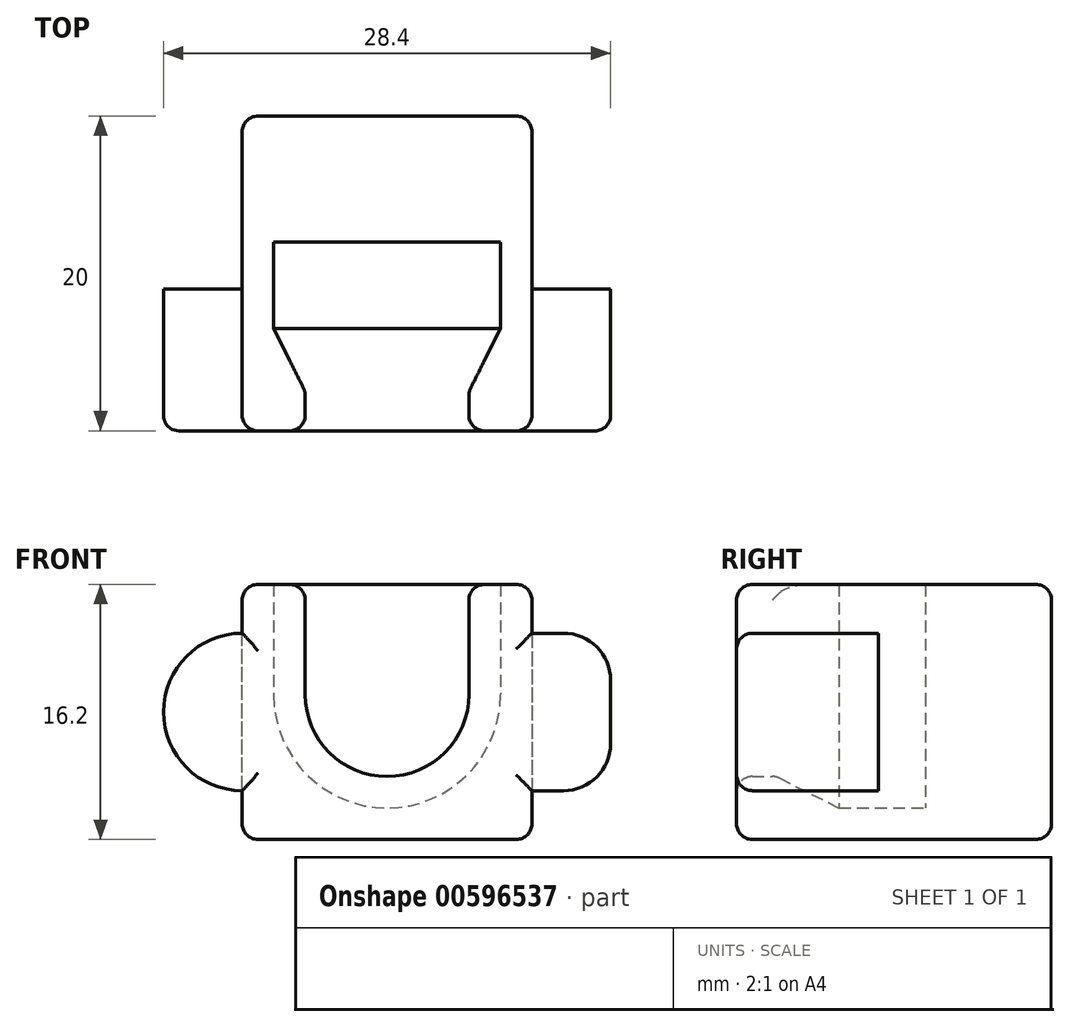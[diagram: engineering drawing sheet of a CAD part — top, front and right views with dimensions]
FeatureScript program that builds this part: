
annotation { "Feature Type Name" : "Feature", "Feature Type Description" : "" }
export const myFeature = defineFeature(function(context is Context, id is Id, definition is map)
    precondition{}
    {
        {
            var Q0;
            Q0=qCreatedBy(makeId("Top.planeOp"),FACE);
            var sketch = newSketch(context, id + "F0", { "sketchPlane" : qUnion([Q0])});
            skLineSegment(sketch, "E0", {"start": v(-9.2, 0) * mm, "end": v(-5.2, 0) * mm});
            skLineSegment(sketch, "E1", {"start": v(-5.2, 0) * mm, "end": v(-5.2, 2.5) * mm});
            skLineSegment(sketch, "E2", {"start": v(-5.2, 2.5) * mm, "end": v(-7.2, 6.5) * mm});
            skLineSegment(sketch, "E3", {"start": v(-7.2, 6.5) * mm, "end": v(-7.2, 12) * mm});
            skLineSegment(sketch, "E4", {"start": v(-7.2, 12) * mm, "end": v(0, 12) * mm});
            skLineSegment(sketch, "E5", {"start": v(0, 12) * mm, "end": v(0, 14) * mm});
            skLineSegment(sketch, "E6", {"start": v(0, 14) * mm, "end": v(-9.2, 14) * mm});
            skLineSegment(sketch, "E7", {"start": v(-9.2, 14) * mm, "end": v(-9.2, 0) * mm});
            skLineSegment(sketch, "E8", {"start": v(0, 44.18) * mm, "end": v(0, -54.71) * mm, "construction": true});
            skSolve(sketch);
        }
        {
            var Q0;
            Q0=makeQuery(id+"F0.imprint","IMPRINT",FACE,{"disambiguationData":[TD([[makeQuery(id+"F0.imprint","IMPRINT",EDGE,{"derivedFrom":sQuery(id+"F0.wireOp",EDGE,"E0")}),1.0]])]});
            var Q1;
            Q1=sQuery(id+"F0.wireOp",EDGE,"E8");
            revolve(context, id + "F1", {"entities" : qUnion([Q0]), "axis" : qUnion([Q1]), "revolveType" : RevolveType.ONE_DIRECTION, "angle" : 180 * degree});
        }
        {
            var Q0;
            Q0=makeQuery(id+"F1.opRevolve","SWEPT_FACE",FACE,{"disambiguationData":[OSD([sQuery(id+"F0.wireOp",EDGE,"E6")])]});
            var sketch = newSketch(context, id + "F2", { "sketchPlane" : qUnion([Q0])});
            skLineSegment(sketch, "E9", {"start": v(-9.2, 0) * mm, "end": v(-9.2, -9.2) * mm});
            skPoint(sketch, "E9.endSnap0", {"position": v(0, -9.2) * mm});
            skLineSegment(sketch, "E10", {"start": v(-9.2, -9.2) * mm, "end": v(9.2, -9.2) * mm});
            skLineSegment(sketch, "E11", {"start": v(9.2, -9.2) * mm, "end": v(9.2, 0) * mm});
            skSolve(sketch);
        }
        {
            var Q0;
            {var subQ0=sQuery(id+"F2.wireOp",EDGE,"E9");Q0=makeQuery(id+"F2.imprint","IMPRINT",FACE,{"disambiguationData":[TD([[makeQuery(id+"F2.imprint","IMPRINT",EDGE,{"derivedFrom":subQ0}),1.0]])]});}
            var Q1;
            {var subQ0=sQuery(id+"F2.wireOp",EDGE,"E11");Q1=makeQuery(id+"F2.imprint","IMPRINT",FACE,{"disambiguationData":[TD([[makeQuery(id+"F2.imprint","IMPRINT",EDGE,{"derivedFrom":subQ0}),1.0]])]});}
            var Q2;
            Q2=makeQuery(id+"F1.opRevolve","SWEPT_FACE",FACE,{"disambiguationData":[OSD([sQuery(id+"F0.wireOp",EDGE,"E0")])]});
            extrude(context, id + "F3", {"entities" : qUnion([Q0, Q1]), "operationType" : NewBodyOperationType.ADD, "endBound" : BoundingType.UP_TO_SURFACE, "oppositeDirection" : true, "depth" : 17 * mm, "endBoundEntityFace" : qUnion([Q2]), "offsetDistance" : 25 * mm});
        }
        {
            var Q0;
            Q0=makeQuery(id+"F1.opRevolve","CAP_FACE",FACE,{"disambiguationData":[OSD([sQuery(id+"F0.wireOp",EDGE,"E0"),sQuery(id+"F0.wireOp",EDGE,"E1"),sQuery(id+"F0.wireOp",EDGE,"E2"),sQuery(id+"F0.wireOp",EDGE,"E3"),sQuery(id+"F0.wireOp",EDGE,"E4"),sQuery(id+"F0.wireOp",EDGE,"E5"),sQuery(id+"F0.wireOp",EDGE,"E6"),sQuery(id+"F0.wireOp",EDGE,"E7")])],"isStart":false});
            extrude(context, id + "F4", {"entities" : qUnion([Q0]), "operationType" : NewBodyOperationType.ADD, "depth" : 7 * mm, "offsetDistance" : 25 * mm});
        }
        {
            var Q0;
            {var subQ0=sQuery(id+"F0.wireOp",EDGE,"E6");var subQ1=sQuery(id+"F2.wireOp",EDGE,"E10");var subQ2=sQuery(id+"F0.wireOp",EDGE,"E7");Q0=makeQuery(id+"F4.boolean.opBoolean","MERGE",FACE,{"derivedFrom":[makeQuery(id+"F3.boolean.opBoolean","MERGE",FACE,{"derivedFrom":[makeQuery(id+"F1.opRevolve","SWEPT_FACE",FACE,{"disambiguationData":[OSD([subQ0])]}),makeQuery(id+"F3.opExtrude","CAP_FACE",FACE,{"disambiguationData":[OSD([subQ0,subQ2,sQuery(id+"F2.wireOp",EDGE,"E9"),subQ1])],"isStart":true}),makeQuery(id+"F3.opExtrude","CAP_FACE",FACE,{"disambiguationData":[OSD([subQ0,subQ2,subQ1,sQuery(id+"F2.wireOp",EDGE,"E11")])],"isStart":true})]}),makeQuery(id+"F4.opExtrude","SWEPT_FACE",FACE,{"disambiguationData":[OSD([subQ0])]})]});}
            var sketch = newSketch(context, id + "F5", { "sketchPlane" : qUnion([Q0])});
            skCircle(sketch, "E12", {"center": v(9.2, -1.1) * mm, "radius": 5 * mm});
            skLineSegment(sketch, "E13.bottom", {"start": v(-11.2, 3.9) * mm, "end": v(-4.2, 3.9) * mm});
            skLineSegment(sketch, "E13.top", {"start": v(-11.2, -6.1) * mm, "end": v(-4.2, -6.1) * mm});
            skLineSegment(sketch, "E13.left", {"start": v(-14.2, 0.9) * mm, "end": v(-14.2, -3.1) * mm});
            skLineSegment(sketch, "E13.right", {"start": v(-4.2, 3.9) * mm, "end": v(-4.2, -6.1) * mm});
            skPoint(sketch, "E13.middle", {"position": v(-9.2, -1.1) * mm});
            skPoint(sketch, "E14.visualSharp", {"position": v(-14.2, -6.1) * mm});
            skArc(sketch, "E14.filletArc", {"start": v(-14.2, -3.1) * mm, "mid": v(-13.32, -5.22) * mm, "end": v(-11.2, -6.1) * mm});
            skPoint(sketch, "E15.visualSharp", {"position": v(-14.2, 3.9) * mm});
            skArc(sketch, "E15.filletArc", {"start": v(-11.2, 3.9) * mm, "mid": v(-13.32, 3.02) * mm, "end": v(-14.2, 0.9) * mm});
            skSolve(sketch);
        }
        {
            var Q0;
            {var subQ0=sQuery(id+"F5.wireOp",EDGE,"E12");var subQ1=sQuery(id+"F2.wireOp",EDGE,"E11");var subQ2=makeQuery(id+"F4.boolean.opBoolean","MERGE",EDGE,{"derivedFrom":[makeQuery(id+"F3.opExtrude","CAP_EDGE",EDGE,{"disambiguationData":[OSD([subQ1])],"isStart":true}),makeQuery(id+"F4.opExtrude","SWEPT_EDGE",EDGE,{"disambiguationData":[OSD([sQuery(id+"F0.wireOp",EDGE,"E6"),sQuery(id+"F0.wireOp",EDGE,"E7"),subQ1])]})]});var subQ3=makeQuery(id+"F5.imprint","INTERSECT",VERTEX,{"disambiguationData":[OD(0.0)],"derivedFrom":[subQ2,subQ0]});Q0=makeQuery(id+"F5.imprint","IMPRINT",FACE,{"disambiguationData":[TD([[makeQuery(id+"F5.imprint","IMPRINT",EDGE,{"disambiguationData":[TD([[subQ3,-1.0]])],"derivedFrom":subQ0}),1.0]])]});}
            var Q1;
            Q1=makeQuery(id+"F5.imprint","IMPRINT",FACE,{"disambiguationData":[TD([[makeQuery(id+"F5.imprint","IMPRINT",EDGE,{"derivedFrom":sQuery(id+"F5.wireOp",EDGE,"E13.left")}),1.0]])]});
            var Q2;
            {var subQ0=sQuery(id+"F0.wireOp",EDGE,"E0");Q2=makeQuery(id+"F4.boolean.opBoolean","MERGE",FACE,{"derivedFrom":[makeQuery(id+"F3.boolean.opBoolean","MERGE",FACE,{"derivedFrom":[makeQuery(id+"F1.opRevolve","SWEPT_FACE",FACE,{"disambiguationData":[OSD([subQ0])]}),makeQuery(id+"F3.opExtrude","CAP_FACE",FACE,{"disambiguationData":[OSD([subQ0]),OD(0.0)],"isStart":false}),makeQuery(id+"F3.opExtrude","CAP_FACE",FACE,{"disambiguationData":[OSD([subQ0]),OD(1.0)],"isStart":false})]}),makeQuery(id+"F4.opExtrude","SWEPT_FACE",FACE,{"disambiguationData":[OSD([subQ0]),TDD([makeQuery(id+"F1.opRevolve","CAP_EDGE",EDGE,{"disambiguationData":[OSD([subQ0])],"isStart":true})])]}),makeQuery(id+"F4.opExtrude","SWEPT_FACE",FACE,{"disambiguationData":[OSD([subQ0]),TDD([makeQuery(id+"F1.opRevolve","CAP_EDGE",EDGE,{"disambiguationData":[OSD([subQ0])],"isStart":false})])]})]});}
            extrude(context, id + "F6", {"entities" : qUnion([Q0, Q1]), "operationType" : NewBodyOperationType.ADD, "endBound" : BoundingType.UP_TO_SURFACE, "oppositeDirection" : true, "depth" : 25 * mm, "endBoundEntityFace" : qUnion([Q2]), "offsetDistance" : 25 * mm});
        }
        {
            var Q0;
            {var subQ0=sQuery(id+"F5.wireOp",EDGE,"E12");var subQ1=sQuery(id+"F2.wireOp",EDGE,"E11");var subQ2=makeQuery(id+"F4.boolean.opBoolean","MERGE",EDGE,{"derivedFrom":[makeQuery(id+"F3.opExtrude","CAP_EDGE",EDGE,{"disambiguationData":[OSD([subQ1])],"isStart":true}),makeQuery(id+"F4.opExtrude","SWEPT_EDGE",EDGE,{"disambiguationData":[OSD([sQuery(id+"F0.wireOp",EDGE,"E6"),sQuery(id+"F0.wireOp",EDGE,"E7"),subQ1])]})]});var subQ3=makeQuery(id+"F5.imprint","INTERSECT",VERTEX,{"disambiguationData":[OD(0.0)],"derivedFrom":[subQ2,subQ0]});Q0=makeQuery(id+"F5.imprint","IMPRINT",FACE,{"disambiguationData":[TD([[makeQuery(id+"F5.imprint","IMPRINT",EDGE,{"disambiguationData":[TD([[subQ3,-1.0]])],"derivedFrom":subQ0}),1.0]])]});}
            var Q1;
            Q1=makeQuery(id+"F5.imprint","IMPRINT",FACE,{"disambiguationData":[TD([[makeQuery(id+"F5.imprint","IMPRINT",EDGE,{"derivedFrom":sQuery(id+"F5.wireOp",EDGE,"E13.left")}),1.0]])]});
            extrude(context, id + "F7", {"entities" : qUnion([Q0, Q1]), "operationType" : NewBodyOperationType.REMOVE, "oppositeDirection" : true, "depth" : 5 * mm, "offsetDistance" : 25 * mm});
        }
        {
            var Q0;
            {var subQ0=sQuery(id+"F5.wireOp",EDGE,"E12");var subQ1=sQuery(id+"F2.wireOp",EDGE,"E11");var subQ2=makeQuery(id+"F4.boolean.opBoolean","MERGE",EDGE,{"derivedFrom":[makeQuery(id+"F3.opExtrude","CAP_EDGE",EDGE,{"disambiguationData":[OSD([subQ1])],"isStart":true}),makeQuery(id+"F4.opExtrude","SWEPT_EDGE",EDGE,{"disambiguationData":[OSD([sQuery(id+"F0.wireOp",EDGE,"E6"),sQuery(id+"F0.wireOp",EDGE,"E7"),subQ1])]})]});var subQ3=makeQuery(id+"F5.imprint","INTERSECT",VERTEX,{"disambiguationData":[OD(0.0)],"derivedFrom":[subQ2,subQ0]});Q0=makeQuery(id+"F5.imprint","IMPRINT",FACE,{"disambiguationData":[TD([[makeQuery(id+"F5.imprint","IMPRINT",EDGE,{"disambiguationData":[TD([[subQ3,1.0]])],"derivedFrom":subQ0}),1.0]])]});}
            var Q1;
            {var subQ0=sQuery(id+"F5.wireOp",EDGE,"E13.right");Q1=makeQuery(id+"F5.imprint","IMPRINT",FACE,{"disambiguationData":[TD([[makeQuery(id+"F5.imprint","IMPRINT",EDGE,{"derivedFrom":subQ0}),1.0]])]});}
            var Q2;
            {var subQ0=sQuery(id+"F5.wireOp",EDGE,"E13.right");Q2=makeQuery(id+"F5.imprint","IMPRINT",FACE,{"disambiguationData":[TD([[makeQuery(id+"F5.imprint","IMPRINT",EDGE,{"derivedFrom":subQ0}),-1.0]])]});}
            extrude(context, id + "F8", {"entities" : qUnion([Q0, Q1, Q2]), "operationType" : NewBodyOperationType.ADD, "depth" : 6 * mm, "offsetDistance" : 25 * mm});
        }
        {
            var Q0;
            Q0=makeQuery(id+"F4.opExtrude","CAP_EDGE",EDGE,{"disambiguationData":[OSD([sQuery(id+"F0.wireOp",EDGE,"E6"),sQuery(id+"F0.wireOp",EDGE,"E7"),sQuery(id+"F2.wireOp",EDGE,"E9")])],"isStart":false});
            var Q1;
            Q1=makeQuery(id+"F4.opExtrude","CAP_EDGE",EDGE,{"disambiguationData":[OSD([sQuery(id+"F0.wireOp",EDGE,"E6"),sQuery(id+"F0.wireOp",EDGE,"E7"),sQuery(id+"F2.wireOp",EDGE,"E11")])],"isStart":false});
            var Q2;
            Q2=makeQuery(id+"F3.opExtrude","SWEPT_EDGE",EDGE,{"disambiguationData":[OSD([sQuery(id+"F2.wireOp",EDGE,"E9"),sQuery(id+"F2.wireOp",EDGE,"E10")])]});
            var Q3;
            Q3=makeQuery(id+"F3.opExtrude","SWEPT_EDGE",EDGE,{"disambiguationData":[OSD([sQuery(id+"F2.wireOp",EDGE,"E10"),sQuery(id+"F2.wireOp",EDGE,"E11")])]});
            var Q4;
            {var subQ0=sQuery(id+"F0.wireOp",EDGE,"E0");Q4=makeQuery(id+"F4.opExtrude","CAP_EDGE",EDGE,{"disambiguationData":[OSD([subQ0]),TDD([makeQuery(id+"F1.opRevolve","CAP_EDGE",EDGE,{"disambiguationData":[OSD([subQ0])],"isStart":false})])],"isStart":false});}
            var Q5;
            {var subQ0=sQuery(id+"F0.wireOp",EDGE,"E0");Q5=makeQuery(id+"F4.opExtrude","CAP_EDGE",EDGE,{"disambiguationData":[OSD([subQ0]),TDD([makeQuery(id+"F1.opRevolve","CAP_EDGE",EDGE,{"disambiguationData":[OSD([subQ0])],"isStart":true})])],"isStart":false});}
            var Q6;
            {var subQ0=sQuery(id+"F2.wireOp",EDGE,"E9");Q6=makeQuery(id+"F4.boolean.opBoolean","MERGE",EDGE,{"derivedFrom":[makeQuery(id+"F3.opExtrude","CAP_EDGE",EDGE,{"disambiguationData":[OSD([subQ0])],"isStart":false}),makeQuery(id+"F4.opExtrude","SWEPT_EDGE",EDGE,{"disambiguationData":[OSD([sQuery(id+"F0.wireOp",EDGE,"E0"),sQuery(id+"F0.wireOp",EDGE,"E6"),sQuery(id+"F0.wireOp",EDGE,"E7"),subQ0])]})]});}
            var Q7;
            {var subQ0=sQuery(id+"F2.wireOp",EDGE,"E11");Q7=makeQuery(id+"F4.boolean.opBoolean","MERGE",EDGE,{"derivedFrom":[makeQuery(id+"F3.opExtrude","CAP_EDGE",EDGE,{"disambiguationData":[OSD([subQ0])],"isStart":false}),makeQuery(id+"F4.opExtrude","SWEPT_EDGE",EDGE,{"disambiguationData":[OSD([sQuery(id+"F0.wireOp",EDGE,"E0"),sQuery(id+"F0.wireOp",EDGE,"E6"),sQuery(id+"F0.wireOp",EDGE,"E7"),subQ0])]})]});}
            var Q8;
            {var subQ0=sQuery(id+"F2.wireOp",EDGE,"E10");Q8=makeQuery(id+"F3.boolean.opBoolean","MERGE",EDGE,{"derivedFrom":[makeQuery(id+"F3.opExtrude","CAP_EDGE",EDGE,{"disambiguationData":[OSD([subQ0]),TDD([makeQuery(id+"F2.imprint","IMPRINT",EDGE,{"disambiguationData":[TD([[makeQuery(id+"F2.imprint","INTERSECT",VERTEX,{"derivedFrom":[sQuery(id+"F2.wireOp",EDGE,"E9"),subQ0]}),-1.0]])],"derivedFrom":subQ0})])],"isStart":false}),makeQuery(id+"F3.opExtrude","CAP_EDGE",EDGE,{"disambiguationData":[OSD([subQ0]),TDD([makeQuery(id+"F2.imprint","IMPRINT",EDGE,{"disambiguationData":[TD([[makeQuery(id+"F2.imprint","INTERSECT",VERTEX,{"derivedFrom":[subQ0,sQuery(id+"F2.wireOp",EDGE,"E11")]}),1.0]])],"derivedFrom":subQ0})])],"isStart":false})]});}
            var Q9;
            {var subQ0=sQuery(id+"F0.wireOp",EDGE,"E6");var subQ1=sQuery(id+"F2.wireOp",EDGE,"E10");var subQ2=sQuery(id+"F0.wireOp",EDGE,"E7");Q9=makeQuery(id+"F4.boolean.opBoolean","MERGE",FACE,{"derivedFrom":[makeQuery(id+"F3.boolean.opBoolean","MERGE",FACE,{"derivedFrom":[makeQuery(id+"F1.opRevolve","SWEPT_FACE",FACE,{"disambiguationData":[OSD([subQ0])]}),makeQuery(id+"F3.opExtrude","CAP_FACE",FACE,{"disambiguationData":[OSD([subQ0,subQ2,sQuery(id+"F2.wireOp",EDGE,"E9"),subQ1])],"isStart":true}),makeQuery(id+"F3.opExtrude","CAP_FACE",FACE,{"disambiguationData":[OSD([subQ0,subQ2,subQ1,sQuery(id+"F2.wireOp",EDGE,"E11")])],"isStart":true})]}),makeQuery(id+"F4.opExtrude","SWEPT_FACE",FACE,{"disambiguationData":[OSD([subQ0])]})]});}
            var Q10;
            {var subQ0=sQuery(id+"F0.wireOp",EDGE,"E0");Q10=makeQuery(id+"F6.boolean.opBoolean","MERGE",FACE,{"derivedFrom":[makeQuery(id+"F4.boolean.opBoolean","MERGE",FACE,{"derivedFrom":[makeQuery(id+"F3.boolean.opBoolean","MERGE",FACE,{"derivedFrom":[makeQuery(id+"F1.opRevolve","SWEPT_FACE",FACE,{"disambiguationData":[OSD([subQ0])]}),makeQuery(id+"F3.opExtrude","CAP_FACE",FACE,{"disambiguationData":[OSD([subQ0]),OD(0.0)],"isStart":false}),makeQuery(id+"F3.opExtrude","CAP_FACE",FACE,{"disambiguationData":[OSD([subQ0]),OD(1.0)],"isStart":false})]}),makeQuery(id+"F4.opExtrude","SWEPT_FACE",FACE,{"disambiguationData":[OSD([subQ0]),TDD([makeQuery(id+"F1.opRevolve","CAP_EDGE",EDGE,{"disambiguationData":[OSD([subQ0])],"isStart":true})])]}),makeQuery(id+"F4.opExtrude","SWEPT_FACE",FACE,{"disambiguationData":[OSD([subQ0]),TDD([makeQuery(id+"F1.opRevolve","CAP_EDGE",EDGE,{"disambiguationData":[OSD([subQ0])],"isStart":false})])]})]}),makeQuery(id+"F6.opExtrude","CAP_FACE",FACE,{"disambiguationData":[OSD([subQ0]),OD(0.0)],"isStart":false}),makeQuery(id+"F6.opExtrude","CAP_FACE",FACE,{"disambiguationData":[OSD([subQ0]),OD(1.0)],"isStart":false})]});}
            var Q11;
            Q11=makeQuery(id+"F8.opExtrude","CAP_FACE",FACE,{"disambiguationData":[OSD([sQuery(id+"F0.wireOp",EDGE,"E6"),sQuery(id+"F0.wireOp",EDGE,"E7"),sQuery(id+"F2.wireOp",EDGE,"E9"),sQuery(id+"F2.wireOp",EDGE,"E10"),sQuery(id+"F2.wireOp",EDGE,"E11")])],"isStart":false});
            var Q12;
            Q12=makeQuery(id+"F7.boolean.opBoolean","COPY",EDGE,{"derivedFrom":makeQuery(id+"F7.opExtrude","CAP_EDGE",EDGE,{"disambiguationData":[OSD([sQuery(id+"F5.wireOp",EDGE,"E12")])],"isStart":false})});
            var Q13;
            Q13=makeQuery(id+"F7.boolean.opBoolean","COPY",EDGE,{"derivedFrom":makeQuery(id+"F7.opExtrude","CAP_EDGE",EDGE,{"disambiguationData":[OSD([sQuery(id+"F5.wireOp",EDGE,"E13.left")])],"isStart":false})});
            var Q14;
            {var subQ0=sQuery(id+"F0.wireOp",EDGE,"E2");var subQ1=sQuery(id+"F0.wireOp",EDGE,"E1");Q14=makeQuery(id+"F4.opExtrude","SWEPT_EDGE",EDGE,{"disambiguationData":[OSD([subQ1,subQ0]),TDD([makeQuery(id+"F1.opRevolve","CAP_VERTEX",VERTEX,{"disambiguationData":[OSD([subQ1,subQ0])],"isStart":false})])]});}
            var Q15;
            {var subQ0=sQuery(id+"F0.wireOp",EDGE,"E1");Q15=makeQuery(id+"F4.opExtrude","CAP_EDGE",EDGE,{"disambiguationData":[OSD([subQ0]),TDD([makeQuery(id+"F1.opRevolve","CAP_EDGE",EDGE,{"disambiguationData":[OSD([subQ0])],"isStart":false})])],"isStart":false});}
            var Q16;
            {var subQ0=sQuery(id+"F0.wireOp",EDGE,"E1");Q16=makeQuery(id+"F4.opExtrude","CAP_EDGE",EDGE,{"disambiguationData":[OSD([subQ0]),TDD([makeQuery(id+"F1.opRevolve","CAP_EDGE",EDGE,{"disambiguationData":[OSD([subQ0])],"isStart":true})])],"isStart":false});}
            fillet(context, id + "F9", {"entities" : qUnion([Q0, Q1, Q2, Q3, Q4, Q5, Q6, Q7, Q8, Q9, Q10, Q11, Q12, Q13, Q14, Q15, Q16]), "radius" : 1 * mm, "tangentPropagation" : true, "allowEdgeOverflow" : false});
        }
    });
